# Revit family: Power-ModularDevices-GEWISS-90RCD-MDC45_4P
name_source: partatom
category: Apparecchi elettrici
revit_build: Autodesk Revit MEP 2016 (Build: 20150220_1215(x64)
units: mm (PartAtom-declared; Revit-internal decimal feet)

## family parameters
Condiviso = Sì
Host = Superficie
Mantenere orientamento annotazione = Sì
Numero OmniClass = 23.80.30.14
Punto di calcolo locali = Sì
Quota connettore circolare = Usa diametro
Taglio con vuoti quando caricato = No
Tipo di parte = Normale
Titolo OmniClass = Power Distribution

## types (1)
- Power-ModularDevices-GEWISS-90RCD-MDC45_4P
    Altezza = 85 mm  [stored 0.278871 ft]
    Assembly position: = Any
    Auxiliaries compatibility = Yes
    Breaking capacity EN 60947-2 (Ics) = 100% Icu
    Breaking capacity EN 60947-2 400V (Icu) = 4,5KA
    Breaking capacity EN 61009-1 (Ics) = 1 x Icn
    Breaking capacity EN 61009-1 400V (Icn) = 4500A
    Carico apparente = 0 VA
    Catalogue = POWER
    Catalogue Range = 90 RCD
    Curve = C
    Description = RCCB WITH OVERCURRENT PROTECTION
    Descrizione = COMPACT RCBO 4P C32 4.5KA A/0.3 4M
    Double connection = YES (only down stream)
    EAN code = 8011564060807
    Electrical endurance = 10000
    Electrocod = 1413
    Finitura = GW - grigio chiaro
    IDF = 4d8b9787-d3c0-4db7-8bdb-0a95d267ba3d
    IDT = df8ad9d6-7a44-4f6f-952b-0f4e7a4b4378
    Idn = 300MA
    Immagine tipo = GW94066.jpg
    Insulation voltage = 500V
    Interuttore = GW - grigio scuro
    Label = MDC 45
    Larghezza = 72 mm  [stored 0.23622 ft]
    Level of immunity (8/20 µs) = 250A
    Mechanical endurance = 20.000
    Modello = GW94280
    No. modules = 4
    No. of modules EN 50022 = 4
    No. of poles = 4P
    Number of poles = 4P
    Numero di poli_ = 3
    Operating temperature = -25 +40 °C
    Overvoltage category = III
    Parti incassate = Sì
    Precision = 300 mA
    Produttore = GEWISS S.p.A.
    Prospetto di default = 1219 mm
    Rated current (In) = 32A
    Rated current: = 32A
    Rated frequency (Hz) = 50/60 Hz
    Rated impulse withstand voltage = 4KV
    Rated insulation voltage (Ui) = 500V
    Rated residual operating current = 300 mA
    Rated tightening torque = 2 Nm
    Rated voltage = 400V
    Rated voltage (EN/IEC 61009-1, 61009-2-1) = 400/415 V
    ReStart compatibility = Yes
    SEO = RCCB
    Section flexible cable = <=1x35 - <=2x16 - <=1x16+2x10 mm²
    Section rigid cable = <=1x35 - <=2x16 - <=1x16+2x10 mm²
    Spessore = 150 mm
    Standard = EN 61009-1
    Standard; = IEC/EN 61009-1, IEC/EN 61009-2-1
    Stocking temperature = -40 +70 °C
    Technical sheet = https://www.gewiss.com
    Type = A
    Type: = A
    URL = https://www.gewiss.com
    Version file RFA = 19.0
    Voltaggio = 400 V

note: [stored X ft] marks values corroborated as IEEE doubles in the binary element streams (Revit-internal decimal feet)

## geometry (parser evidence)
native form markers: Sweep x1
no freeform markers — native parametric forms only
